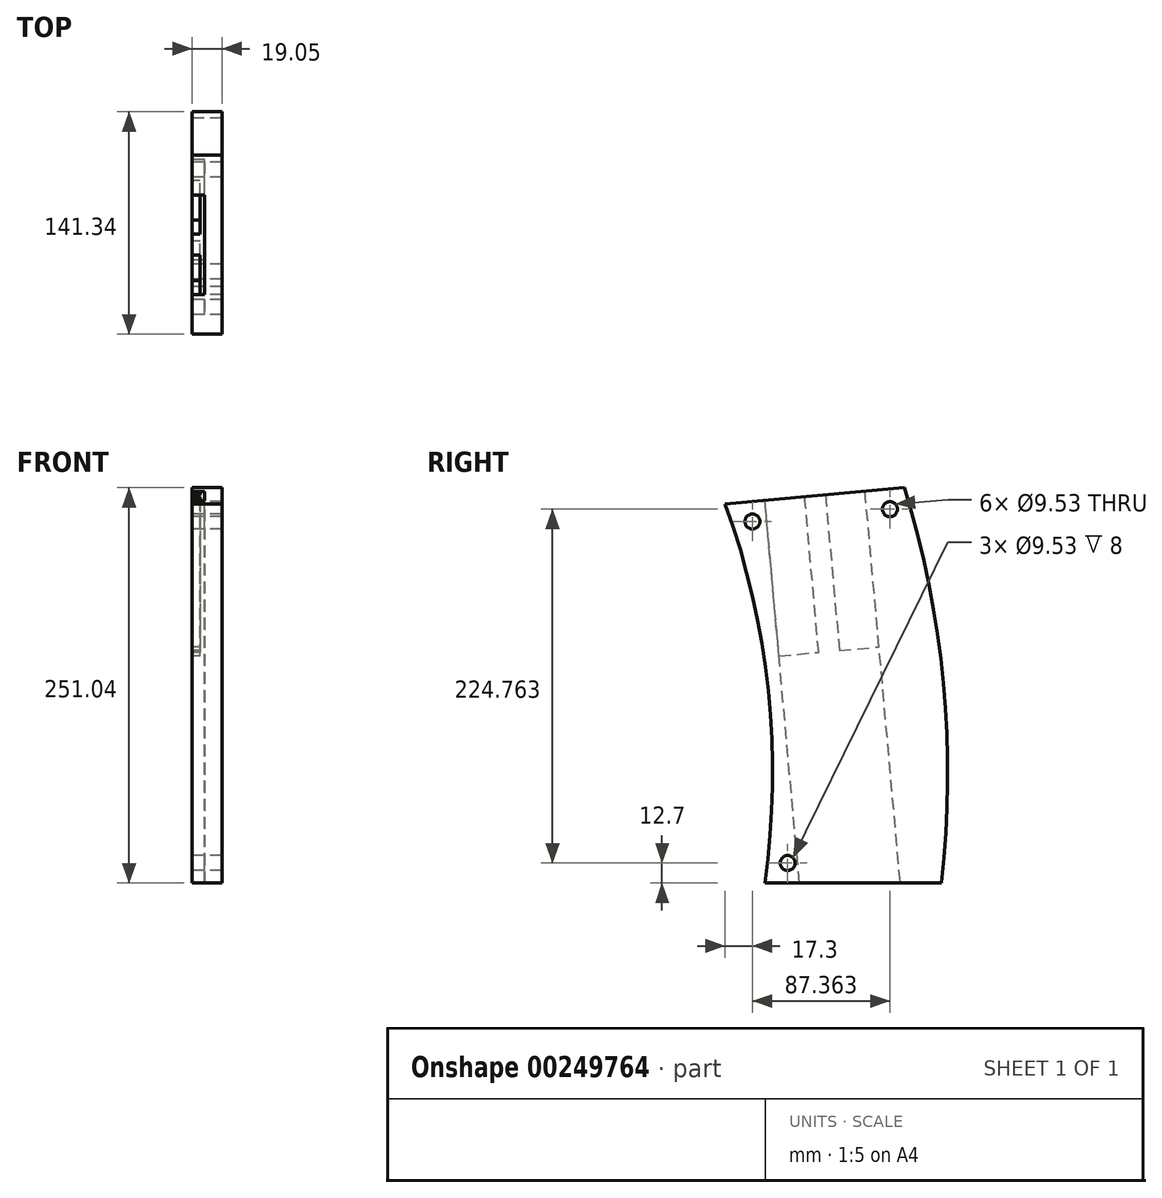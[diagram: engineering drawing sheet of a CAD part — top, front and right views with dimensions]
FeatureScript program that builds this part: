
annotation { "Feature Type Name" : "Feature", "Feature Type Description" : "" }
export const myFeature = defineFeature(function(context is Context, id is Id, definition is map)
    precondition{}
    {
        {
            var Q0;
            Q0=qCreatedBy(makeId("Right.planeOp"),FACE);
            var sketch = newSketch(context, id + "F0", { "sketchPlane" : qUnion([Q0])});
            skLineSegment(sketch, "E0", {"start": v(0, 0) * mm, "end": v(112.08, 0) * mm});
            skArc(sketch, "E1", {"start": v(0, 0) * mm, "mid": v(2.1, 121.94) * mm, "end": v(-25.3, 240.78) * mm});
            skArc(sketch, "E2", {"start": v(112.08, 0) * mm, "mid": v(113.36, 126.74) * mm, "end": v(88.54, 251.04) * mm});
            skLineSegment(sketch, "E3", {"start": v(-43.98, 292.23) * mm, "end": v(-25.3, 240.78) * mm, "construction": true});
            skPoint(sketch, "E4", {"position": v(-25.3, 240.78) * mm});
            skLineSegment(sketch, "E5", {"start": v(88.54, 251.04) * mm, "end": v(-25.3, 240.78) * mm});
            skLineSegment(sketch, "E6", {"start": v(63.24, 248.76) * mm, "end": v(86.04, -4.21) * mm});
            skLineSegment(sketch, "E7", {"start": v(22.8, -9.91) * mm, "end": v(86.04, -4.21) * mm});
            skLineSegment(sketch, "E8", {"start": v(22.8, -9.91) * mm, "end": v(0, 243.06) * mm});
            skArc(sketch, "E9", {"start": v(12.82, 0) * mm, "mid": v(14.8, 122.48) * mm, "end": v(-12.23, 241.96) * mm, "construction": true});
            skArc(sketch, "E10", {"start": v(99.3, 0) * mm, "mid": v(100.66, 126.2) * mm, "end": v(75.6, 249.88) * mm, "construction": true});
            skLineSegment(sketch, "E11", {"start": v(1.61, 12.7) * mm, "end": v(113.4, 12.7) * mm, "construction": true});
            skLineSegment(sketch, "E12", {"start": v(-20.99, 228.42) * mm, "end": v(92.25, 238.62) * mm, "construction": true});
            skCircle(sketch, "E13", {"center": v(-8, 229.6) * mm, "radius": 4.76 * mm});
            skCircle(sketch, "E14", {"center": v(79.36, 237.46) * mm, "radius": 4.76 * mm});
            skCircle(sketch, "E15", {"center": v(14.4, 12.7) * mm, "radius": 4.76 * mm});
            skLineSegment(sketch, "E16", {"start": v(38.34, 246.52) * mm, "end": v(47.25, 147.72) * mm});
            skLineSegment(sketch, "E17", {"start": v(8.9, 144.26) * mm, "end": v(72.15, 149.96) * mm});
            skLineSegment(sketch, "E18", {"start": v(24.9, 245.3) * mm, "end": v(33.8, 146.5) * mm});
            skSolve(sketch);
        }
        {
            var Q0;
            {var subQ4=sQuery(id+"F0.wireOp",EDGE,"E2");Q0=makeQuery(id+"F0.imprint","IMPRINT",FACE,{"disambiguationData":[TD([[makeQuery(id+"F0.imprint","IMPRINT",EDGE,{"derivedFrom":subQ4}),1.0]])]});}
            var Q1;
            {var subQ1=sQuery(id+"F0.wireOp",EDGE,"E8");var subQ4=sQuery(id+"F0.wireOp",EDGE,"E0");var subQ5=makeQuery(id+"F0.imprint","INTERSECT",VERTEX,{"derivedFrom":[subQ4,subQ1]});Q1=makeQuery(id+"F0.imprint","IMPRINT",FACE,{"disambiguationData":[TD([[makeQuery(id+"F0.imprint","IMPRINT",EDGE,{"disambiguationData":[TD([[subQ5,-1.0]])],"derivedFrom":subQ4}),1.0]])]});}
            var Q2;
            {var subQ3=sQuery(id+"F0.wireOp",EDGE,"E18");Q2=makeQuery(id+"F0.imprint","IMPRINT",FACE,{"disambiguationData":[TD([[makeQuery(id+"F0.imprint","IMPRINT",EDGE,{"derivedFrom":subQ3}),-1.0]])]});}
            var Q3;
            {var subQ3=sQuery(id+"F0.wireOp",EDGE,"E16");Q3=makeQuery(id+"F0.imprint","IMPRINT",FACE,{"disambiguationData":[TD([[makeQuery(id+"F0.imprint","IMPRINT",EDGE,{"derivedFrom":subQ3}),1.0]])]});}
            var Q4;
            {var subQ0=sQuery(id+"F0.wireOp",EDGE,"E16");Q4=makeQuery(id+"F0.imprint","IMPRINT",FACE,{"disambiguationData":[TD([[makeQuery(id+"F0.imprint","IMPRINT",EDGE,{"derivedFrom":subQ0}),-1.0]])]});}
            var Q5;
            Q5=makeQuery(id+"F0.imprint","IMPRINT",FACE,{"disambiguationData":[TD([[makeQuery(id+"F0.imprint","IMPRINT",EDGE,{"derivedFrom":sQuery(id+"F0.wireOp",EDGE,"E14")}),1.0]])]});
            var Q6;
            {var subQ5=sQuery(id+"F0.wireOp",EDGE,"E1");Q6=makeQuery(id+"F0.imprint","IMPRINT",FACE,{"disambiguationData":[TD([[makeQuery(id+"F0.imprint","IMPRINT",EDGE,{"derivedFrom":subQ5}),-1.0]])]});}
            var Q7;
            Q7=makeQuery(id+"F0.imprint","IMPRINT",FACE,{"disambiguationData":[TD([[makeQuery(id+"F0.imprint","IMPRINT",EDGE,{"derivedFrom":sQuery(id+"F0.wireOp",EDGE,"E15")}),1.0]])]});
            var Q8;
            Q8=makeQuery(id+"F0.imprint","IMPRINT",FACE,{"disambiguationData":[TD([[makeQuery(id+"F0.imprint","IMPRINT",EDGE,{"derivedFrom":sQuery(id+"F0.wireOp",EDGE,"E13")}),1.0]])]});
            extrude(context, id + "F1", {"entities" : qUnion([Q0, Q1, Q2, Q3, Q4, Q5, Q6, Q7, Q8]), "depth" : 19.05 * mm});
        }
        {
            var Q0;
            Q0=makeQuery(id+"F0.imprint","IMPRINT",FACE,{"disambiguationData":[TD([[makeQuery(id+"F0.imprint","IMPRINT",EDGE,{"derivedFrom":sQuery(id+"F0.wireOp",EDGE,"E14")}),1.0]])]});
            var Q1;
            Q1=makeQuery(id+"F0.imprint","IMPRINT",FACE,{"disambiguationData":[TD([[makeQuery(id+"F0.imprint","IMPRINT",EDGE,{"derivedFrom":sQuery(id+"F0.wireOp",EDGE,"E13")}),1.0]])]});
            var Q2;
            Q2=makeQuery(id+"F0.imprint","IMPRINT",FACE,{"disambiguationData":[TD([[makeQuery(id+"F0.imprint","IMPRINT",EDGE,{"derivedFrom":sQuery(id+"F0.wireOp",EDGE,"E15")}),1.0]])]});
            extrude(context, id + "F2", {"entities" : qUnion([Q0, Q1, Q2]), "operationType" : NewBodyOperationType.REMOVE, "depth" : 8 * mm});
        }
        {
            var Q0;
            {var subQ4=sQuery(id+"F0.wireOp",EDGE,"E2");Q0=makeQuery(id+"F0.imprint","IMPRINT",FACE,{"disambiguationData":[TD([[makeQuery(id+"F0.imprint","IMPRINT",EDGE,{"derivedFrom":subQ4}),1.0]])]});}
            var Q1;
            {var subQ3=sQuery(id+"F0.wireOp",EDGE,"E16");Q1=makeQuery(id+"F0.imprint","IMPRINT",FACE,{"disambiguationData":[TD([[makeQuery(id+"F0.imprint","IMPRINT",EDGE,{"derivedFrom":subQ3}),1.0]])]});}
            var Q2;
            {var subQ0=sQuery(id+"F0.wireOp",EDGE,"E16");Q2=makeQuery(id+"F0.imprint","IMPRINT",FACE,{"disambiguationData":[TD([[makeQuery(id+"F0.imprint","IMPRINT",EDGE,{"derivedFrom":subQ0}),-1.0]])]});}
            var Q3;
            {var subQ3=sQuery(id+"F0.wireOp",EDGE,"E18");Q3=makeQuery(id+"F0.imprint","IMPRINT",FACE,{"disambiguationData":[TD([[makeQuery(id+"F0.imprint","IMPRINT",EDGE,{"derivedFrom":subQ3}),-1.0]])]});}
            var Q4;
            {var subQ5=sQuery(id+"F0.wireOp",EDGE,"E1");Q4=makeQuery(id+"F0.imprint","IMPRINT",FACE,{"disambiguationData":[TD([[makeQuery(id+"F0.imprint","IMPRINT",EDGE,{"derivedFrom":subQ5}),-1.0]])]});}
            var Q5;
            {var subQ1=sQuery(id+"F0.wireOp",EDGE,"E8");var subQ4=sQuery(id+"F0.wireOp",EDGE,"E0");var subQ5=makeQuery(id+"F0.imprint","INTERSECT",VERTEX,{"derivedFrom":[subQ4,subQ1]});Q5=makeQuery(id+"F0.imprint","IMPRINT",FACE,{"disambiguationData":[TD([[makeQuery(id+"F0.imprint","IMPRINT",EDGE,{"disambiguationData":[TD([[subQ5,-1.0]])],"derivedFrom":subQ4}),1.0]])]});}
            extrude(context, id + "F3", {"entities" : qUnion([Q0, Q1, Q2, Q3, Q4, Q5]), "depth" : 19.05 * mm});
        }
        {
            var Q0;
            {var subQ1=sQuery(id+"F0.wireOp",EDGE,"E8");var subQ4=sQuery(id+"F0.wireOp",EDGE,"E0");var subQ5=makeQuery(id+"F0.imprint","INTERSECT",VERTEX,{"derivedFrom":[subQ4,subQ1]});Q0=makeQuery(id+"F0.imprint","IMPRINT",FACE,{"disambiguationData":[TD([[makeQuery(id+"F0.imprint","IMPRINT",EDGE,{"disambiguationData":[TD([[subQ5,-1.0]])],"derivedFrom":subQ4}),1.0]])]});}
            var Q1;
            {var subQ3=sQuery(id+"F0.wireOp",EDGE,"E16");Q1=makeQuery(id+"F0.imprint","IMPRINT",FACE,{"disambiguationData":[TD([[makeQuery(id+"F0.imprint","IMPRINT",EDGE,{"derivedFrom":subQ3}),1.0]])]});}
            var Q2;
            {var subQ0=sQuery(id+"F0.wireOp",EDGE,"E16");Q2=makeQuery(id+"F0.imprint","IMPRINT",FACE,{"disambiguationData":[TD([[makeQuery(id+"F0.imprint","IMPRINT",EDGE,{"derivedFrom":subQ0}),-1.0]])]});}
            var Q3;
            {var subQ3=sQuery(id+"F0.wireOp",EDGE,"E18");Q3=makeQuery(id+"F0.imprint","IMPRINT",FACE,{"disambiguationData":[TD([[makeQuery(id+"F0.imprint","IMPRINT",EDGE,{"derivedFrom":subQ3}),-1.0]])]});}
            extrude(context, id + "F4", {"entities" : qUnion([Q0, Q1, Q2, Q3]), "operationType" : NewBodyOperationType.REMOVE, "depth" : 8 * mm});
        }
        {
            var Q0;
            {var subQ1=sQuery(id+"F0.wireOp",EDGE,"E8");var subQ4=sQuery(id+"F0.wireOp",EDGE,"E0");var subQ5=makeQuery(id+"F0.imprint","INTERSECT",VERTEX,{"derivedFrom":[subQ4,subQ1]});Q0=makeQuery(id+"F0.imprint","IMPRINT",FACE,{"disambiguationData":[TD([[makeQuery(id+"F0.imprint","IMPRINT",EDGE,{"disambiguationData":[TD([[subQ5,-1.0]])],"derivedFrom":subQ4}),1.0]])]});}
            var Q1;
            {var subQ4=sQuery(id+"F0.wireOp",EDGE,"E2");Q1=makeQuery(id+"F0.imprint","IMPRINT",FACE,{"disambiguationData":[TD([[makeQuery(id+"F0.imprint","IMPRINT",EDGE,{"derivedFrom":subQ4}),1.0]])]});}
            var Q2;
            {var subQ3=sQuery(id+"F0.wireOp",EDGE,"E16");Q2=makeQuery(id+"F0.imprint","IMPRINT",FACE,{"disambiguationData":[TD([[makeQuery(id+"F0.imprint","IMPRINT",EDGE,{"derivedFrom":subQ3}),1.0]])]});}
            var Q3;
            {var subQ0=sQuery(id+"F0.wireOp",EDGE,"E16");Q3=makeQuery(id+"F0.imprint","IMPRINT",FACE,{"disambiguationData":[TD([[makeQuery(id+"F0.imprint","IMPRINT",EDGE,{"derivedFrom":subQ0}),-1.0]])]});}
            var Q4;
            {var subQ3=sQuery(id+"F0.wireOp",EDGE,"E18");Q4=makeQuery(id+"F0.imprint","IMPRINT",FACE,{"disambiguationData":[TD([[makeQuery(id+"F0.imprint","IMPRINT",EDGE,{"derivedFrom":subQ3}),-1.0]])]});}
            var Q5;
            {var subQ5=sQuery(id+"F0.wireOp",EDGE,"E1");Q5=makeQuery(id+"F0.imprint","IMPRINT",FACE,{"disambiguationData":[TD([[makeQuery(id+"F0.imprint","IMPRINT",EDGE,{"derivedFrom":subQ5}),-1.0]])]});}
            extrude(context, id + "F5", {"entities" : qUnion([Q0, Q1, Q2, Q3, Q4, Q5]), "depth" : 19.05 * mm});
        }
        {
            var Q0;
            {var subQ3=sQuery(id+"F0.wireOp",EDGE,"E16");Q0=makeQuery(id+"F0.imprint","IMPRINT",FACE,{"disambiguationData":[TD([[makeQuery(id+"F0.imprint","IMPRINT",EDGE,{"derivedFrom":subQ3}),1.0]])]});}
            var Q1;
            {var subQ3=sQuery(id+"F0.wireOp",EDGE,"E18");Q1=makeQuery(id+"F0.imprint","IMPRINT",FACE,{"disambiguationData":[TD([[makeQuery(id+"F0.imprint","IMPRINT",EDGE,{"derivedFrom":subQ3}),-1.0]])]});}
            extrude(context, id + "F6", {"entities" : qUnion([Q0, Q1]), "operationType" : NewBodyOperationType.REMOVE, "depth" : 5 * mm});
        }
    });
